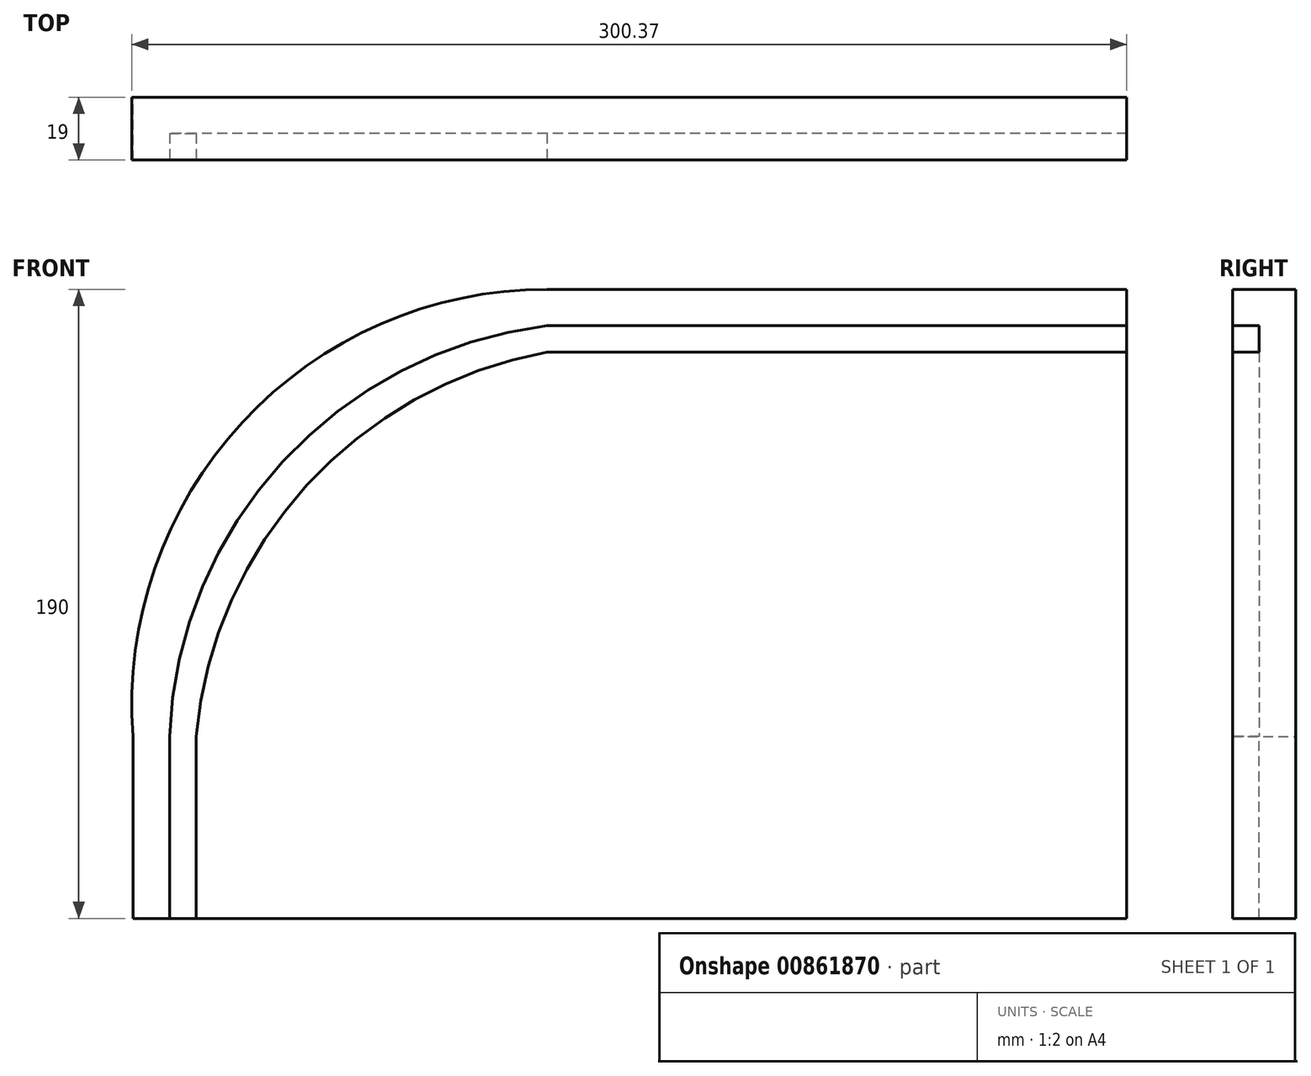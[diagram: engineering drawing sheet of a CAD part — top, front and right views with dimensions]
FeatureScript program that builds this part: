
annotation { "Feature Type Name" : "Feature", "Feature Type Description" : "" }
export const myFeature = defineFeature(function(context is Context, id is Id, definition is map)
    precondition{}
    {
        {
            var Q0;
            Q0=qCreatedBy(makeId("Front.planeOp"),FACE);
            var sketch = newSketch(context, id + "F0", { "sketchPlane" : qUnion([Q0])});
            skLineSegment(sketch, "E0", {"start": v(-300, 55) * mm, "end": v(-300, 0) * mm});
            skLineSegment(sketch, "E1", {"start": v(-300, 0) * mm, "end": v(0, 0) * mm});
            skLineSegment(sketch, "E2", {"start": v(0, 0) * mm, "end": v(0, 190) * mm});
            skLineSegment(sketch, "E3", {"start": v(0, 190) * mm, "end": v(-175, 190) * mm});
            skArc(sketch, "E4", {"start": v(-175, 190) * mm, "mid": v(-267, 149.8) * mm, "end": v(-300, 55) * mm});
            skSolve(sketch);
        }
        {
            var Q0;
            Q0=makeQuery(id+"F0.imprint","IMPRINT",FACE,{"disambiguationData":[TD([[makeQuery(id+"F0.imprint","IMPRINT",EDGE,{"derivedFrom":sQuery(id+"F0.wireOp",EDGE,"E0")}),1.0]])]});
            extrude(context, id + "F1", {"entities" : qUnion([Q0]), "depth" : 19 * mm, "offsetDistance" : 25.4 * mm});
        }
        {
            var Q0;
            Q0=makeQuery(id+"F1.opExtrude","CAP_FACE",FACE,{"disambiguationData":[OSD([sQuery(id+"F0.wireOp",EDGE,"E0"),sQuery(id+"F0.wireOp",EDGE,"E1"),sQuery(id+"F0.wireOp",EDGE,"E2"),sQuery(id+"F0.wireOp",EDGE,"E3"),sQuery(id+"F0.wireOp",EDGE,"E4")])],"isStart":false});
            var sketch = newSketch(context, id + "F2", { "sketchPlane" : qUnion([Q0])});
            skPoint(sketch, "E5", {"position": v(0, 179) * mm});
            skPoint(sketch, "E6", {"position": v(0, 171) * mm});
            skLineSegment(sketch, "E7", {"start": v(0, 179) * mm, "end": v(-175, 179) * mm});
            skLineSegment(sketch, "E8", {"start": v(0, 171) * mm, "end": v(-175, 171) * mm});
            skPoint(sketch, "E9", {"position": v(-289, 0) * mm});
            skPoint(sketch, "E10", {"position": v(-281, 0) * mm});
            skLineSegment(sketch, "E11", {"start": v(-289, 0) * mm, "end": v(-289, 55) * mm});
            skLineSegment(sketch, "E12", {"start": v(-281, 0) * mm, "end": v(-281, 55) * mm});
            skArc(sketch, "E13", {"start": v(-175, 171) * mm, "mid": v(-247.5, 130.83) * mm, "end": v(-281, 55) * mm});
            skArc(sketch, "E14", {"start": v(-175, 179) * mm, "mid": v(-254.8, 137.96) * mm, "end": v(-289, 55) * mm});
            skSolve(sketch);
        }
        {
            var Q0;
            {var subQ1=sQuery(id+"F2.wireOp",EDGE,"E7");Q0=makeQuery(id+"F2.imprint","IMPRINT",FACE,{"disambiguationData":[TD([[makeQuery(id+"F2.imprint","IMPRINT",EDGE,{"derivedFrom":subQ1}),1.0]])]});}
            extrude(context, id + "F3", {"entities" : qUnion([Q0]), "operationType" : NewBodyOperationType.REMOVE, "oppositeDirection" : true, "depth" : 8 * mm, "offsetDistance" : 25 * mm});
        }
    });
